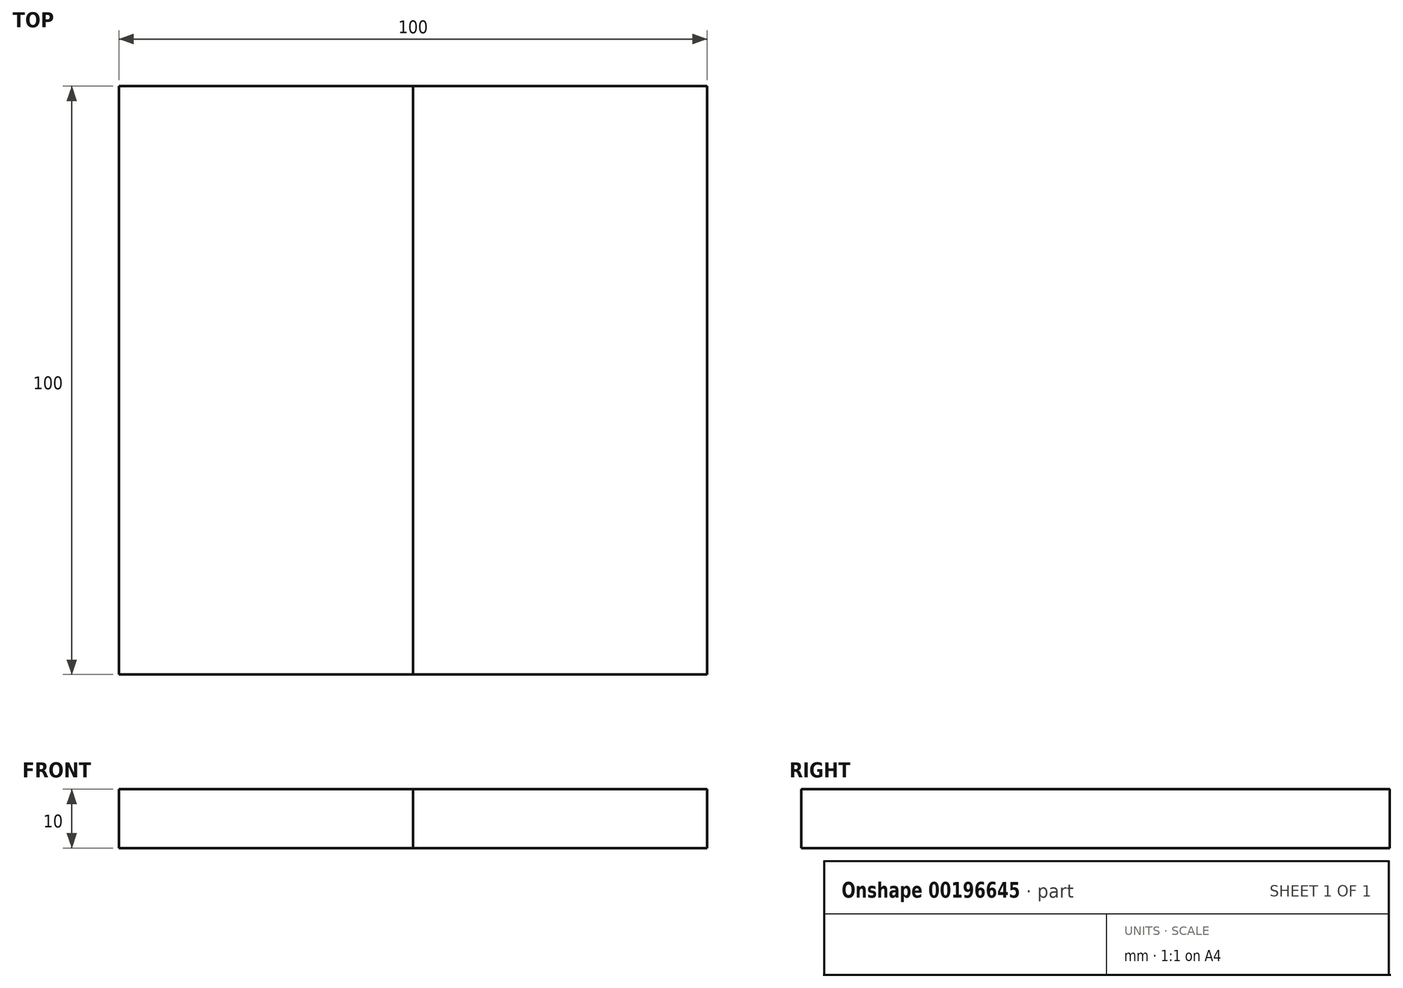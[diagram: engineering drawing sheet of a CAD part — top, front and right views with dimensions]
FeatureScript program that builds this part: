
annotation { "Feature Type Name" : "Feature", "Feature Type Description" : "" }
export const myFeature = defineFeature(function(context is Context, id is Id, definition is map)
    precondition{}
    {
        {
            var Q0;
            Q0=qCreatedBy(makeId("Top.planeOp"),FACE);
            var sketch = newSketch(context, id + "F0", { "sketchPlane" : qUnion([Q0])});
            skLineSegment(sketch, "E0.bottom", {"start": v(0, 0) * mm, "end": v(50, 0) * mm});
            skLineSegment(sketch, "E0.top", {"start": v(0, 100) * mm, "end": v(50, 100) * mm});
            skLineSegment(sketch, "E0.left", {"start": v(0, 0) * mm, "end": v(0, 100) * mm});
            skLineSegment(sketch, "E0.right", {"start": v(50, 0) * mm, "end": v(50, 100) * mm});
            skSolve(sketch);
        }
        {
            var Q0;
            Q0=makeQuery(id+"F0.imprint","IMPRINT",FACE,{"disambiguationData":[TD([[makeQuery(id+"F0.imprint","IMPRINT",EDGE,{"derivedFrom":sQuery(id+"F0.wireOp",EDGE,"E0.bottom")}),1.0]])]});
            extrude(context, id + "F1", {"entities" : qUnion([Q0]), "depth" : 10 * mm});
        }
        {
            var Q0;
            Q0=makeQuery(id+"F1.opExtrude","SWEPT_BODY",BODY,{"disambiguationData":[OSD([sQuery(id+"F0.wireOp",EDGE,"E0.bottom"),sQuery(id+"F0.wireOp",EDGE,"E0.top"),sQuery(id+"F0.wireOp",EDGE,"E0.left"),sQuery(id+"F0.wireOp",EDGE,"E0.right")])]});
            transform(context, id + "F2", {"entities" : qUnion([Q0]), "transformType" : TransformType.TRANSLATION_3D, "dx" : 50 * mm, "dy" : 0 * mm, "dz" : 0 * mm, "makeCopy" : true});
        }
    });
